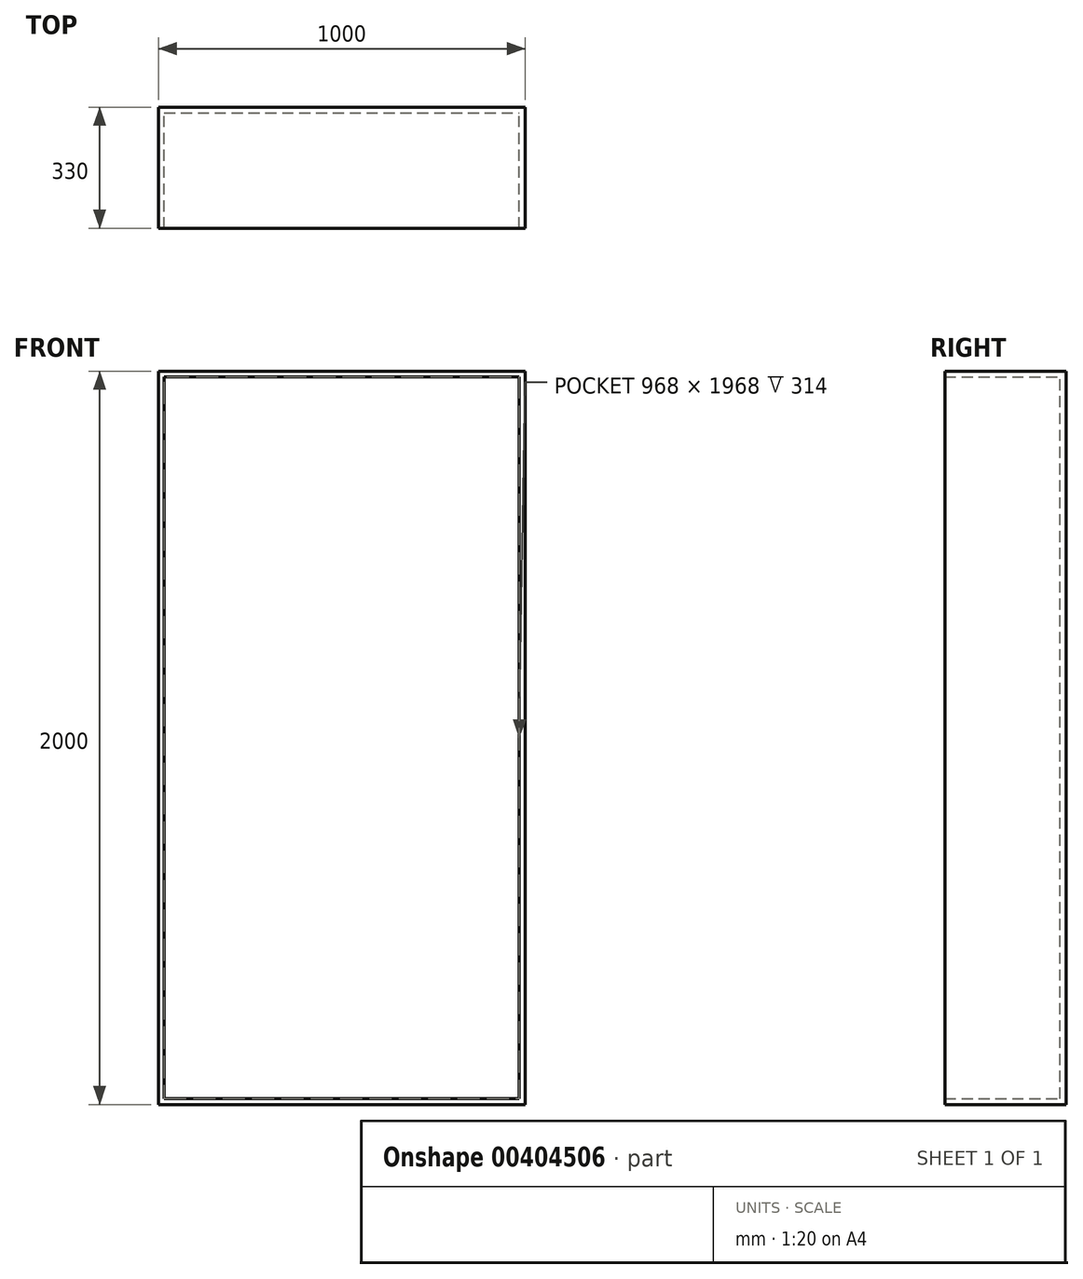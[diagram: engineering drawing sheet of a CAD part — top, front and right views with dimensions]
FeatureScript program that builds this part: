
annotation { "Feature Type Name" : "Feature", "Feature Type Description" : "" }
export const myFeature = defineFeature(function(context is Context, id is Id, definition is map)
    precondition{}
    {
        {
            var Q0;
            Q0=qCreatedBy(makeId("Front.planeOp"),FACE);
            var sketch = newSketch(context, id + "F0", { "sketchPlane" : qUnion([Q0])});
            skLineSegment(sketch, "E0.bottom", {"start": v(0, 0) * mm, "end": v(52.06, 0) * mm});
            skLineSegment(sketch, "E0.top", {"start": v(0, 50.23) * mm, "end": v(52.06, 50.23) * mm});
            skLineSegment(sketch, "E0.left", {"start": v(0, 0) * mm, "end": v(0, 50.23) * mm});
            skLineSegment(sketch, "E0.right", {"start": v(52.06, 0) * mm, "end": v(52.06, 50.23) * mm});
            skSolve(sketch);
        }
        {
            var Q0;
            Q0=makeQuery(id+"F0.imprint","IMPRINT",FACE,{"disambiguationData":[TD([[makeQuery(id+"F0.imprint","IMPRINT",EDGE,{"derivedFrom":sQuery(id+"F0.wireOp",EDGE,"E0.bottom")}),1.0]])]});
            extrude(context, id + "F1", {"entities" : qUnion([Q0]), "depth" : 330 * mm});
        }
        {
            var Q0;
            Q0=makeQuery(id+"F1.opExtrude","SWEPT_FACE",FACE,{"disambiguationData":[OSD([sQuery(id+"F0.wireOp",EDGE,"E0.left")])]});
            extrude(context, id + "F2", {"entities" : qUnion([Q0]), "operationType" : NewBodyOperationType.ADD, "oppositeDirection" : true, "depth" : 2000 * mm});
        }
        {
            var Q0;
            {var subQ0=sQuery(id+"F0.wireOp",EDGE,"E0.bottom");Q0=makeQuery(id+"F2.boolean.opBoolean","MERGE",FACE,{"derivedFrom":[makeQuery(id+"F1.opExtrude","SWEPT_FACE",FACE,{"disambiguationData":[OSD([subQ0])]}),makeQuery(id+"F2.opExtrude","SWEPT_FACE",FACE,{"disambiguationData":[OSD([subQ0,sQuery(id+"F0.wireOp",EDGE,"E0.left")])]})]});}
            extrude(context, id + "F3", {"entities" : qUnion([Q0]), "operationType" : NewBodyOperationType.ADD, "oppositeDirection" : true, "depth" : 2000 * mm});
        }
        {
            var Q0;
            {var subQ0=sQuery(id+"F0.wireOp",EDGE,"E0.left");var subQ1=sQuery(id+"F0.wireOp",EDGE,"E0.bottom");Q0=makeQuery(id+"F3.boolean.opBoolean","MERGE",FACE,{"derivedFrom":[makeQuery(id+"F1.opExtrude","SWEPT_FACE",FACE,{"disambiguationData":[OSD([subQ0])]}),makeQuery(id+"F3.opExtrude","SWEPT_FACE",FACE,{"disambiguationData":[OSD([subQ1,subQ0]),TDD([makeQuery(id+"F1.opExtrude","SWEPT_EDGE",EDGE,{"disambiguationData":[OSD([subQ1,subQ0])]})])]})]});}
            extrude(context, id + "F4", {"entities" : qUnion([Q0]), "operationType" : NewBodyOperationType.INTERSECT, "oppositeDirection" : true, "depth" : 1000 * mm});
        }
        {
            var Q0;
            {var subQ0=sQuery(id+"F0.wireOp",EDGE,"E0.left");var subQ1=sQuery(id+"F0.wireOp",EDGE,"E0.bottom");Q0=makeQuery(id+"F3.boolean.opBoolean","MERGE",FACE,{"derivedFrom":[makeQuery(id+"F2.boolean.opBoolean","MERGE",FACE,{"derivedFrom":[makeQuery(id+"F1.opExtrude","CAP_FACE",FACE,{"disambiguationData":[OSD([subQ1,sQuery(id+"F0.wireOp",EDGE,"E0.top"),subQ0,sQuery(id+"F0.wireOp",EDGE,"E0.right")])],"isStart":false}),makeQuery(id+"F2.opExtrude","SWEPT_FACE",FACE,{"disambiguationData":[OSD([subQ0]),TDD([makeQuery(id+"F1.opExtrude","CAP_EDGE",EDGE,{"disambiguationData":[OSD([subQ0])],"isStart":false})])]})]}),makeQuery(id+"F3.opExtrude","SWEPT_FACE",FACE,{"disambiguationData":[OSD([subQ1,subQ0]),TDD([makeQuery(id+"F2.boolean.opBoolean","MERGE",EDGE,{"derivedFrom":[makeQuery(id+"F1.opExtrude","CAP_EDGE",EDGE,{"disambiguationData":[OSD([subQ1])],"isStart":false}),makeQuery(id+"F2.opExtrude","SWEPT_EDGE",EDGE,{"disambiguationData":[OSD([subQ1,subQ0]),TDD([makeQuery(id+"F1.opExtrude","CAP_VERTEX",VERTEX,{"disambiguationData":[OSD([subQ1,subQ0])],"isStart":false})])]})]})])]})]});}
            shell(context, id + "F5", {"entities" : qUnion([Q0]), "thickness" : 16 * mm});
        }
    });
